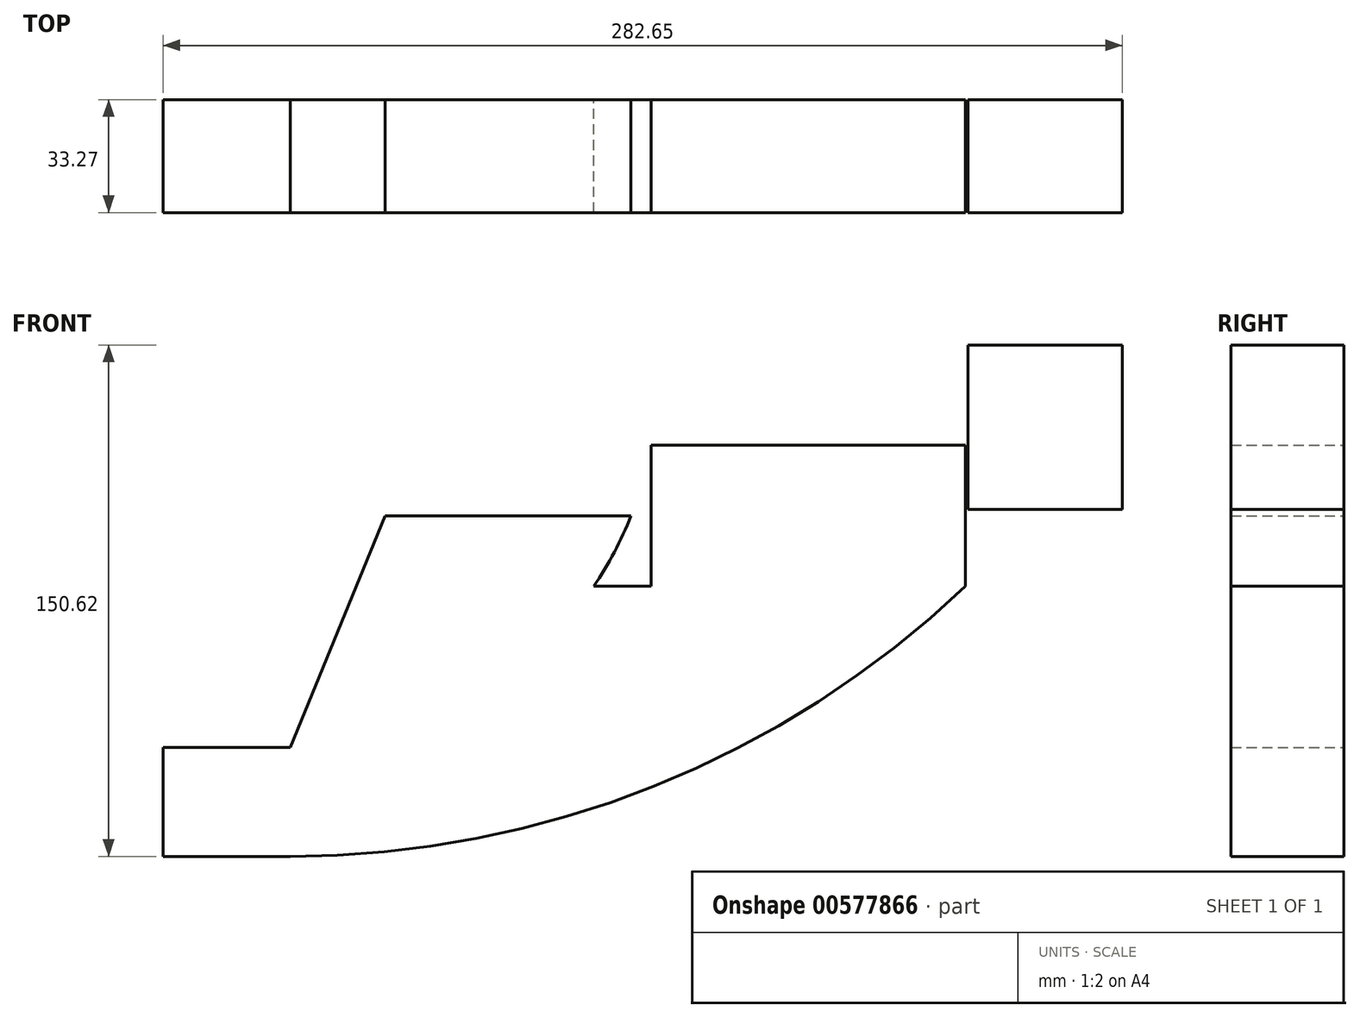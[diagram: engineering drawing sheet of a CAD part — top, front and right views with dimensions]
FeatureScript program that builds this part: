
annotation { "Feature Type Name" : "Feature", "Feature Type Description" : "" }
export const myFeature = defineFeature(function(context is Context, id is Id, definition is map)
    precondition{}
    {
        {
            var Q0;
            Q0=qCreatedBy(makeId("Front.planeOp"),FACE);
            var sketch = newSketch(context, id + "F0", { "sketchPlane" : qUnion([Q0])});
            skLineSegment(sketch, "E0.bottom", {"start": v(-46.26, -20.77) * mm, "end": v(46.26, -20.77) * mm});
            skLineSegment(sketch, "E0.top", {"start": v(-46.26, 20.77) * mm, "end": v(46.26, 20.77) * mm});
            skLineSegment(sketch, "E0.left", {"start": v(-46.26, -20.77) * mm, "end": v(-46.26, 20.77) * mm});
            skLineSegment(sketch, "E0.right", {"start": v(46.26, -20.77) * mm, "end": v(46.26, 20.77) * mm});
            skPoint(sketch, "E0.middle", {"position": v(0, 0) * mm});
            skLineSegment(sketch, "E1.bottom", {"start": v(92.59, 1.87) * mm, "end": v(47.1, 1.87) * mm});
            skLineSegment(sketch, "E1.top", {"start": v(92.59, 50.32) * mm, "end": v(47.1, 50.32) * mm});
            skLineSegment(sketch, "E1.left", {"start": v(92.59, 1.87) * mm, "end": v(92.59, 50.32) * mm});
            skLineSegment(sketch, "E1.right", {"start": v(47.1, 1.87) * mm, "end": v(47.1, 50.32) * mm});
            skPoint(sketch, "E1.middle", {"position": v(69.84, 26.1) * mm});
            skLineSegment(sketch, "E2.bottom", {"start": v(-152.52, -100.3) * mm, "end": v(-190.06, -100.3) * mm});
            skLineSegment(sketch, "E2.top", {"start": v(-152.52, -68.17) * mm, "end": v(-190.06, -68.17) * mm});
            skLineSegment(sketch, "E2.left", {"start": v(-152.52, -100.3) * mm, "end": v(-152.52, -68.17) * mm});
            skLineSegment(sketch, "E2.right", {"start": v(-190.06, -100.3) * mm, "end": v(-190.06, -68.17) * mm});
            skPoint(sketch, "E2.middle", {"position": v(-171.3, -84.23) * mm});
            skLineSegment(sketch, "E3", {"start": v(46.26, 1.87) * mm, "end": v(46.26, 20.77) * mm});
            skLineSegment(sketch, "E4", {"start": v(-46.26, -20.77) * mm, "end": v(-124.57, -20.77) * mm});
            skLineSegment(sketch, "E5", {"start": v(-124.57, -20.77) * mm, "end": v(-152.52, -68.17) * mm});
            skLineSegment(sketch, "E6", {"start": v(-152.52, -68.17) * mm, "end": v(-124.57, 0) * mm});
            skLineSegment(sketch, "E7", {"start": v(-124.57, 0) * mm, "end": v(0, 0) * mm});
            skArc(sketch, "E8", {"start": v(-152.52, -68.17) * mm, "mid": v(-83.24, -43) * mm, "end": v(-46.26, 20.77) * mm});
            skArc(sketch, "E9", {"start": v(-190.06, -68.17) * mm, "mid": v(-108.11, 64.39) * mm, "end": v(47.1, 50.32) * mm});
            skArc(sketch, "E10", {"start": v(-152.52, -100.3) * mm, "mid": v(-45.47, -79.68) * mm, "end": v(46.26, -20.77) * mm});
            skArc(sketch, "E11", {"start": v(47.1, 50.32) * mm, "mid": v(44.12, 53.3) * mm, "end": v(47.1, 56.26) * mm});
            skSolve(sketch);
        }
        {
            var Q0;
            {var subQ0=sQuery(id+"F0.wireOp",EDGE,"E5");Q0=makeQuery(id+"F0.imprint","IMPRINT",FACE,{"disambiguationData":[TD([[makeQuery(id+"F0.imprint","IMPRINT",EDGE,{"derivedFrom":subQ0}),1.0]])]});}
            var Q1;
            {var subQ1=sQuery(id+"F0.wireOp",EDGE,"E0.bottom");Q1=makeQuery(id+"F0.imprint","IMPRINT",FACE,{"disambiguationData":[TD([[makeQuery(id+"F0.imprint","IMPRINT",EDGE,{"derivedFrom":subQ1}),-1.0]])]});}
            var Q2;
            {var subQ3=sQuery(id+"F0.wireOp",EDGE,"E0.bottom");Q2=makeQuery(id+"F0.imprint","IMPRINT",FACE,{"disambiguationData":[TD([[makeQuery(id+"F0.imprint","IMPRINT",EDGE,{"derivedFrom":subQ3}),1.0]])]});}
            var Q3;
            {var subQ4=sQuery(id+"F0.wireOp",EDGE,"E5");Q3=makeQuery(id+"F0.imprint","IMPRINT",FACE,{"disambiguationData":[TD([[makeQuery(id+"F0.imprint","IMPRINT",EDGE,{"derivedFrom":subQ4}),-1.0]])]});}
            var Q4;
            Q4=makeQuery(id+"F0.imprint","IMPRINT",FACE,{"disambiguationData":[TD([[makeQuery(id+"F0.imprint","IMPRINT",EDGE,{"derivedFrom":sQuery(id+"F0.wireOp",EDGE,"E1.bottom")}),-1.0]])]});
            var Q5;
            Q5=makeQuery(id+"F0.imprint","IMPRINT",FACE,{"disambiguationData":[TD([[makeQuery(id+"F0.imprint","IMPRINT",EDGE,{"derivedFrom":sQuery(id+"F0.wireOp",EDGE,"E2.bottom")}),-1.0]])]});
            extrude(context, id + "F1", {"entities" : qUnion([Q0, Q1, Q2, Q3, Q4, Q5]), "depth" : 33.27 * mm, "offsetDistance" : 25.4 * mm});
        }
    });
